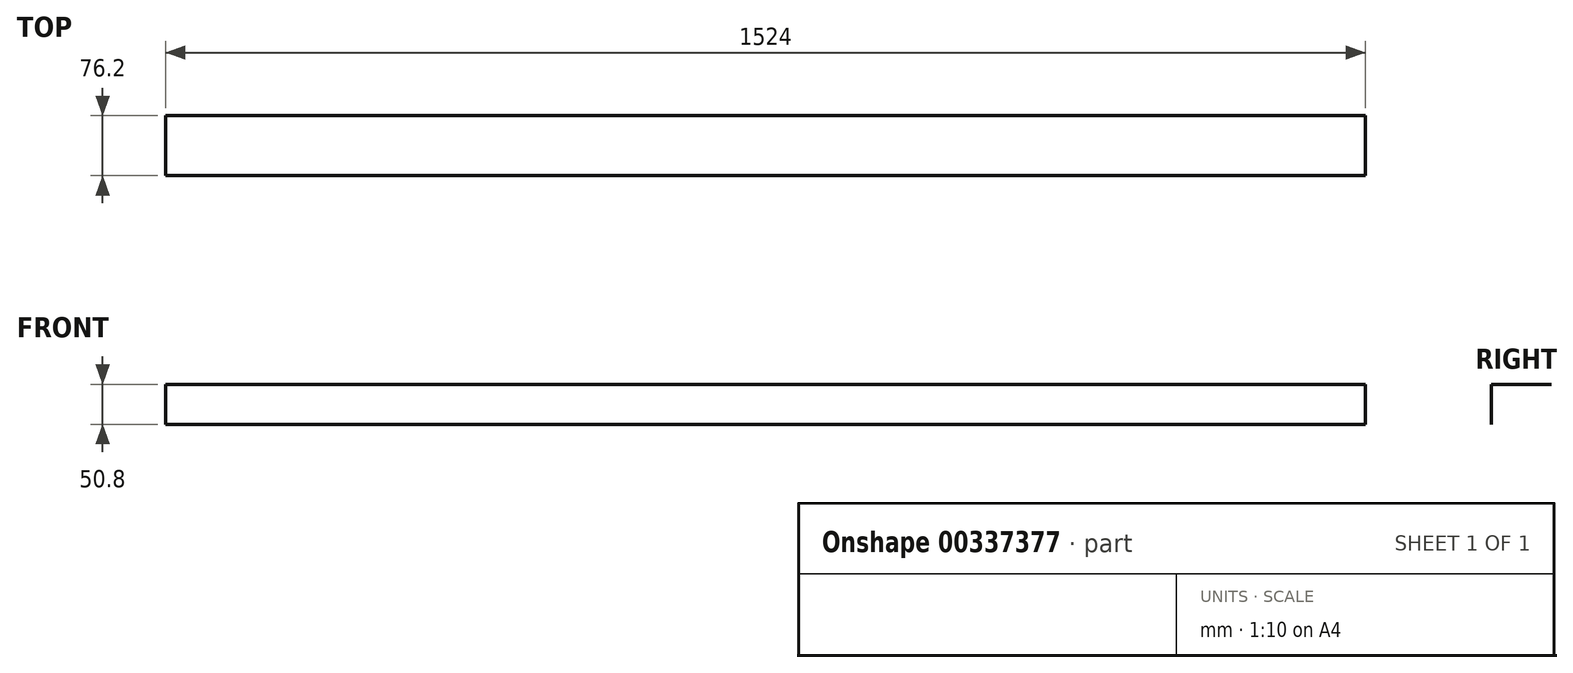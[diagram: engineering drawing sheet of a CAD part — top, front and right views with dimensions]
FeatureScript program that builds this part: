
annotation { "Feature Type Name" : "Feature", "Feature Type Description" : "" }
export const myFeature = defineFeature(function(context is Context, id is Id, definition is map)
    precondition{}
    {
        {
            var Q0;
            Q0=qCreatedBy(makeId("Right.planeOp"),FACE);
            var sketch = newSketch(context, id + "F0", { "sketchPlane" : qUnion([Q0])});
            skLineSegment(sketch, "E0", {"start": v(-92.96, -73.56) * mm, "end": v(-92.96, -22.76) * mm});
            skLineSegment(sketch, "E1", {"start": v(-92.96, -22.76) * mm, "end": v(-16.76, -22.76) * mm});
            skSolve(sketch);
        }
        {
            var Q0;
            Q0 = qSketchRegion(id + "F0", true);
            var Q1;
            Q1=sQuery(id+"F0.wireOp",EDGE,"E1");
            var Q2;
            Q2=sQuery(id+"F0.wireOp",EDGE,"E0");
            extrude(context, id + "F1", {"entities" : qUnion([Q0]), "bodyType" : ToolBodyType.SURFACE, "surfaceEntities" : qUnion([Q1, Q2]), "depth" : 1524 * mm});
        }
    });
